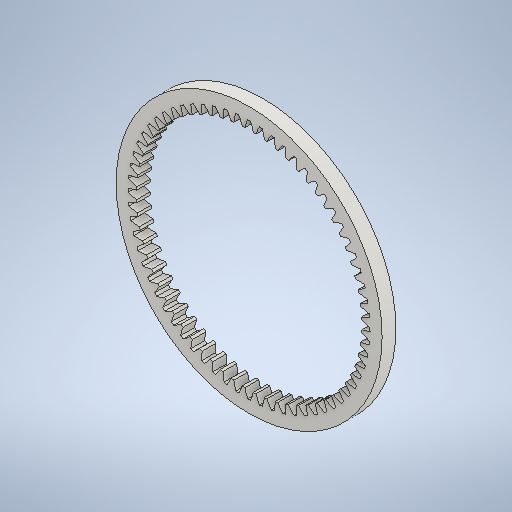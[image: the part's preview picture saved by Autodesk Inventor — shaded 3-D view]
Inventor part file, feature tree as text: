
AUTODESK INVENTOR PART (.ipt)
format: ipt  version: 2025.1 (Build 291241000, 241)  size: 576,000 bytes
history: native  units: mm (DEFAULTED — no unit token found)
features: plane x3, other x3, sketch x2, extrude x1
ambient origin geometry x8: Origin, YZ Plane, XZ Plane, XY Plane, X Axis, Y Axis, Z Axis, Center Point
bodies: Solid1 (feature_tree)
feature tree (9):
  extrude  "Extrusion1"  Depth=7.0mm TaperAngle=0.0deg
  plane  "Work Plane2"
  plane  "Work Plane8"
  plane  "Work Plane9"
  other  "Spur Gear"
  sketch  "Sketch3"  dims[d3=118.4mm d4=10.0mm d5=0.0mm d16=29.6mm d17=0.0mm d34=0.490874mm d39=0.0mm d45=0.0mm d47=29.6mm d50=0.0mm d51=0.0mm d52=29.6mm d53=120.0mm]
  sketch  "Sketch1"  dims[d0=135.3275mm d1=7.0mm d2=0.0mm]
  other  "Srf1"
  other  "Pitch Diameter"
